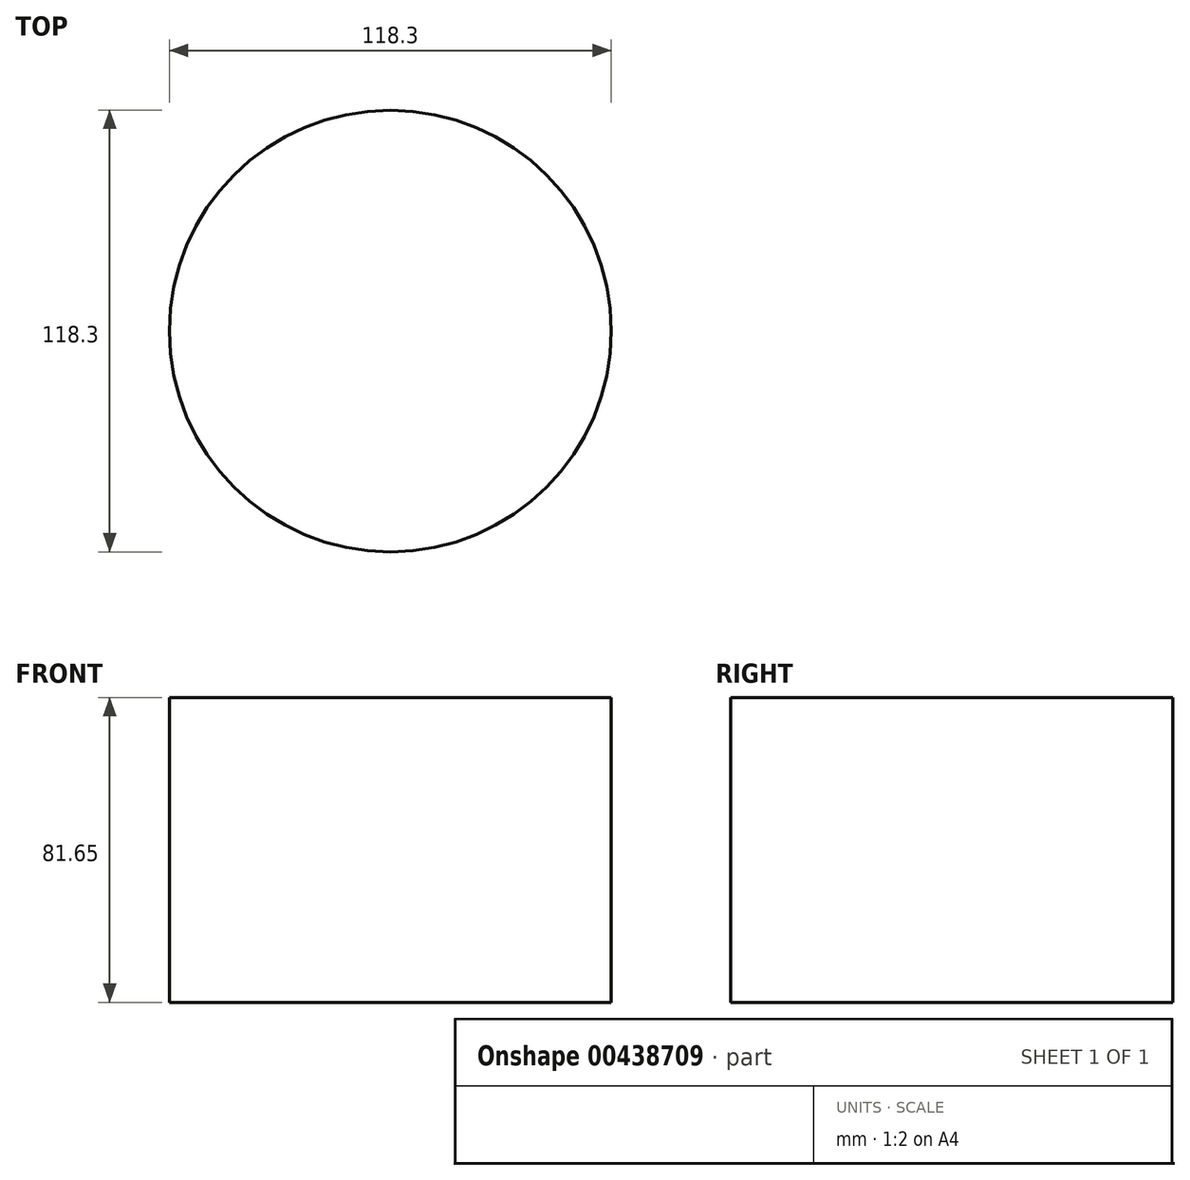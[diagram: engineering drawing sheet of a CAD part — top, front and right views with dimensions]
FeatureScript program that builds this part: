
annotation { "Feature Type Name" : "Feature", "Feature Type Description" : "" }
export const myFeature = defineFeature(function(context is Context, id is Id, definition is map)
    precondition{}
    {
        {
            var Q0;
            Q0=qCreatedBy(makeId("Top.planeOp"),FACE);
            var sketch = newSketch(context, id + "F0", { "sketchPlane" : qUnion([Q0])});
            skCircle(sketch, "E0", {"center": v(0, 0) * mm, "radius": 59.15 * mm});
            skSolve(sketch);
        }
        {
            var Q0;
            Q0=makeQuery(id+"F0.imprint","IMPRINT",FACE,{"disambiguationData":[TD([[makeQuery(id+"F0.imprint","IMPRINT",EDGE,{"derivedFrom":sQuery(id+"F0.wireOp",EDGE,"E0")}),1.0]])]});
            var sketch = newSketch(context, id + "F1", { "sketchPlane" : qUnion([Q0])});
            skSolve(sketch);
        }
        {
            var Q0;
            Q0 = qSketchRegion(id + "F1", true);
            var Q1;
            Q1=makeQuery(id+"F0.imprint","IMPRINT",FACE,{"disambiguationData":[TD([[makeQuery(id+"F0.imprint","IMPRINT",EDGE,{"derivedFrom":sQuery(id+"F0.wireOp",EDGE,"E0")}),1.0]])]});
            extrude(context, id + "F2", {"entities" : qUnion([Q0, Q1]), "depth" : 81.65 * mm});
        }
    });
